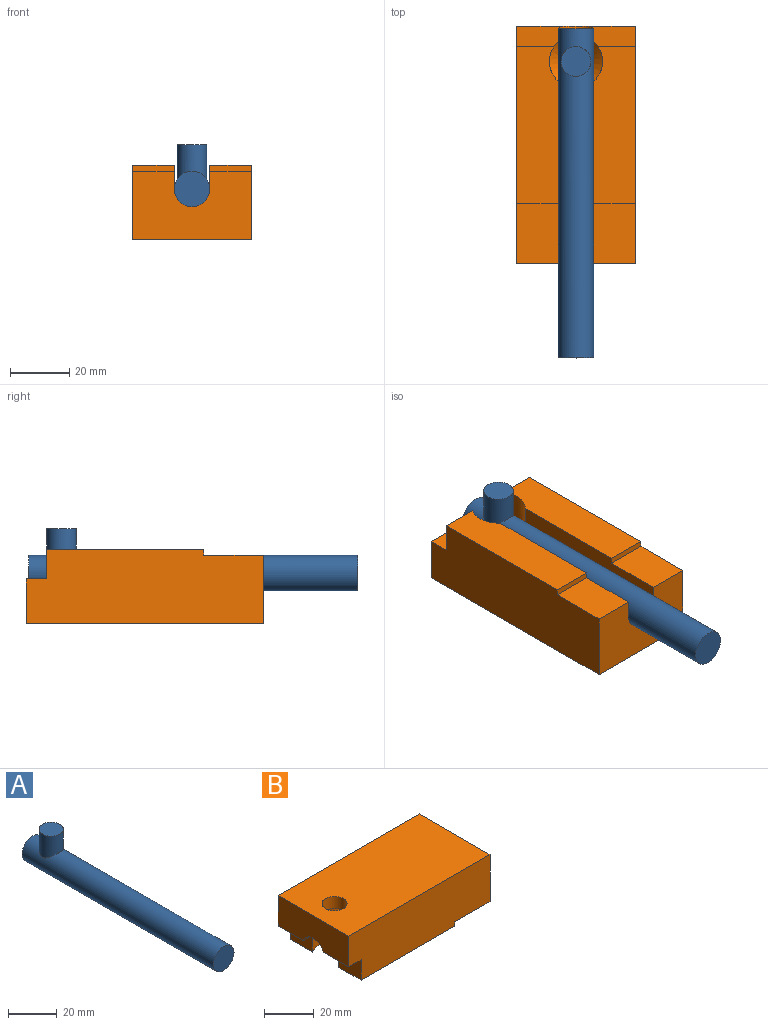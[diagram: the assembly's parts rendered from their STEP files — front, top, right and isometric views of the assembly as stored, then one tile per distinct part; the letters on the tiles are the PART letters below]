
ASSEMBLY  parts=2 mates=1
PART A: 5 faces, bbox 12x111x21 mm
  f0: cylinder r=6mm len=111mm, axis (0,1,0), area 4096.3mm2, adj f1,f2,f3
  f1: plane 12x12mm, normal (0,-1,0), area 113.1mm2, adj f0
  f2: plane 12x12mm, normal (0,1,0), area 113.1mm2, adj f0
  f3: cylinder r=5mm len=11.68mm, axis (0,0,-1), area 321.8mm2, adj f0,f4
  f4: plane 10x10mm, normal (0,0,1), area 78.5mm2, adj f3
PART B: 22 faces, bbox 80x40x25 mm
  f0: plane 53x14mm, normal (0,0,-1), area 715.5mm2, adj f1,f3,f12,f14,f19
  f1: plane 80x25mm, normal (0,1,0), area 1890mm2, adj f0,f6,f8,f9,f13,f14,f18,f19
  f2: plane 53x14mm, normal (0,0,-1), area 715.5mm2, adj f3,f7,f11,f15,f20
  f3: cylinder r=9mm len=18mm, axis (0,0,-1), area 471.3mm2, adj f0,f2,f4,f10,f11,f12,f13,f14
  f4: cylinder r=6mm len=11.31mm, axis (-1,0,0), area 56.2mm2, adj f3,f6,f13,f16
  f5: cylinder r=5mm len=10mm, axis (0,0,1), area 188.5mm2, adj f9,f17
  f6: plane 40x15mm, normal (-1,0,0), area 567mm2, adj f1,f4,f7,f9,f13,f16
  f7: plane 80x25mm, normal (0,-1,0), area 1890mm2, adj f2,f6,f8,f9,f15,f16,f20,f21
  f8: plane 40x23mm, normal (1,0,0), area 791.5mm2, adj f1,f7,f9,f10,f11,f12,f18,f21
  f9: plane 80x40mm, normal (0,0,1), area 3121.5mm2, adj f1,f5,f6,f7,f8
  f10: cylinder r=6mm len=61.29mm, axis (-1,0,0), area 1132.9mm2, adj f3,f8,f11,f12
  f11: plane 61.29x8mm, normal (0,1,0), area 450.3mm2, adj f2,f3,f8,f10,f20,f21
  f12: plane 61.29x8mm, normal (0,-1,0), area 450.3mm2, adj f0,f3,f8,f10,f18,f19
  f13: plane 14.34x7mm, normal (0,0,-1), area 98.4mm2, adj f1,f3,f4,f6,f14
  f14: plane 12.52x10mm, normal (-1,0,0), area 125.2mm2, adj f0,f1,f3,f13
  f15: plane 12.52x10mm, normal (-1,0,0), area 125.2mm2, adj f2,f3,f7,f16
  f16: plane 14.34x7mm, normal (0,0,-1), area 98.4mm2, adj f3,f4,f6,f7,f15
  f17: cone r=9mm half-angle=45deg, axis (0,0,-1), area 248.8mm2, adj f3,f5
  f18: plane 20x14mm, normal (0,0,-1), area 280mm2, adj f1,f8,f12,f19
  f19: plane 14x2mm, normal (1,0,0), area 28mm2, adj f0,f1,f12,f18
  f20: plane 14x2mm, normal (1,0,0), area 28mm2, adj f2,f7,f11,f21
  f21: plane 20x14mm, normal (0,0,-1), area 280mm2, adj f7,f8,f11,f20
PLACE A at identity fixed
PLACE B rot(axis=(-0.71,0.71,0),180deg) t=(20,12,8)mm
MATE fastened B.f4 <-> A.f0  axis (0,1,0) through (0,12,0)mm
